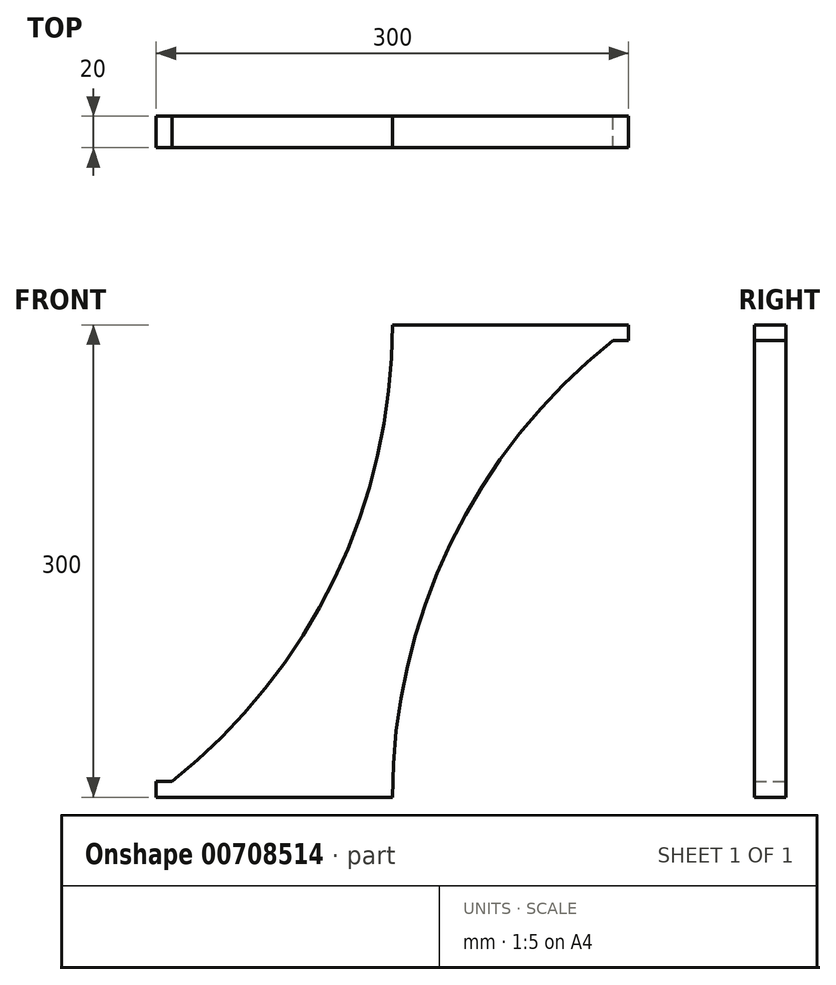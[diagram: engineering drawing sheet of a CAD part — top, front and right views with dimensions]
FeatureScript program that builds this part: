
annotation { "Feature Type Name" : "Feature", "Feature Type Description" : "" }
export const myFeature = defineFeature(function(context is Context, id is Id, definition is map)
    precondition{}
    {
        {
            var Q0;
            Q0=qCreatedBy(makeId("Front.planeOp"),FACE);
            var sketch = newSketch(context, id + "F0", { "sketchPlane" : qUnion([Q0])});
            skPoint(sketch, "E0.start.orphan", {"position": v(682.2, 671.17) * mm});
            skPoint(sketch, "E1.end.orphan", {"position": v(44.74, 0) * mm});
            skPoint(sketch, "E1.start.orphan", {"position": v(637.46, 671.17) * mm});
            skPoint(sketch, "E2.end.orphan", {"position": v(592.72, 671.17) * mm});
            skPoint(sketch, "E3.orphan", {"position": v(89.49, 0) * mm});
            skPoint(sketch, "E4.end.orphan", {"position": v(0, 0) * mm});
            skLineSegment(sketch, "E5", {"start": v(0, 0) * mm, "end": v(150, 0) * mm});
            skPoint(sketch, "E6.start.orphan", {"position": v(156.16, 0) * mm});
            skPoint(sketch, "E7.end.orphan", {"position": v(156.16, -19.62) * mm});
            skLineSegment(sketch, "E8", {"start": v(150, 0) * mm, "end": v(150, 300) * mm});
            skLineSegment(sketch, "E9", {"start": v(150, 300) * mm, "end": v(300, 300) * mm});
            skLineSegment(sketch, "E10", {"start": v(0, 0) * mm, "end": v(0, 10) * mm});
            skLineSegment(sketch, "E11", {"start": v(0, 10) * mm, "end": v(10, 10) * mm});
            skArc(sketch, "E12", {"start": v(10, 10) * mm, "mid": v(113.17, 138.99) * mm, "end": v(150, 300) * mm});
            skLineSegment(sketch, "E13", {"start": v(300, 300) * mm, "end": v(300, 290) * mm});
            skLineSegment(sketch, "E14", {"start": v(300, 290) * mm, "end": v(290, 290) * mm});
            skArc(sketch, "E15", {"start": v(290, 290) * mm, "mid": v(186.83, 161.01) * mm, "end": v(150, 0) * mm});
            skSolve(sketch);
        }
        {
            var Q0;
            Q0=qSketchRegion(id+"F0",true);
            extrude(context, id + "F1", {"entities" : qUnion([Q0]), "depth" : 20 * mm, "offsetDistance" : 25 * mm});
        }
    });
